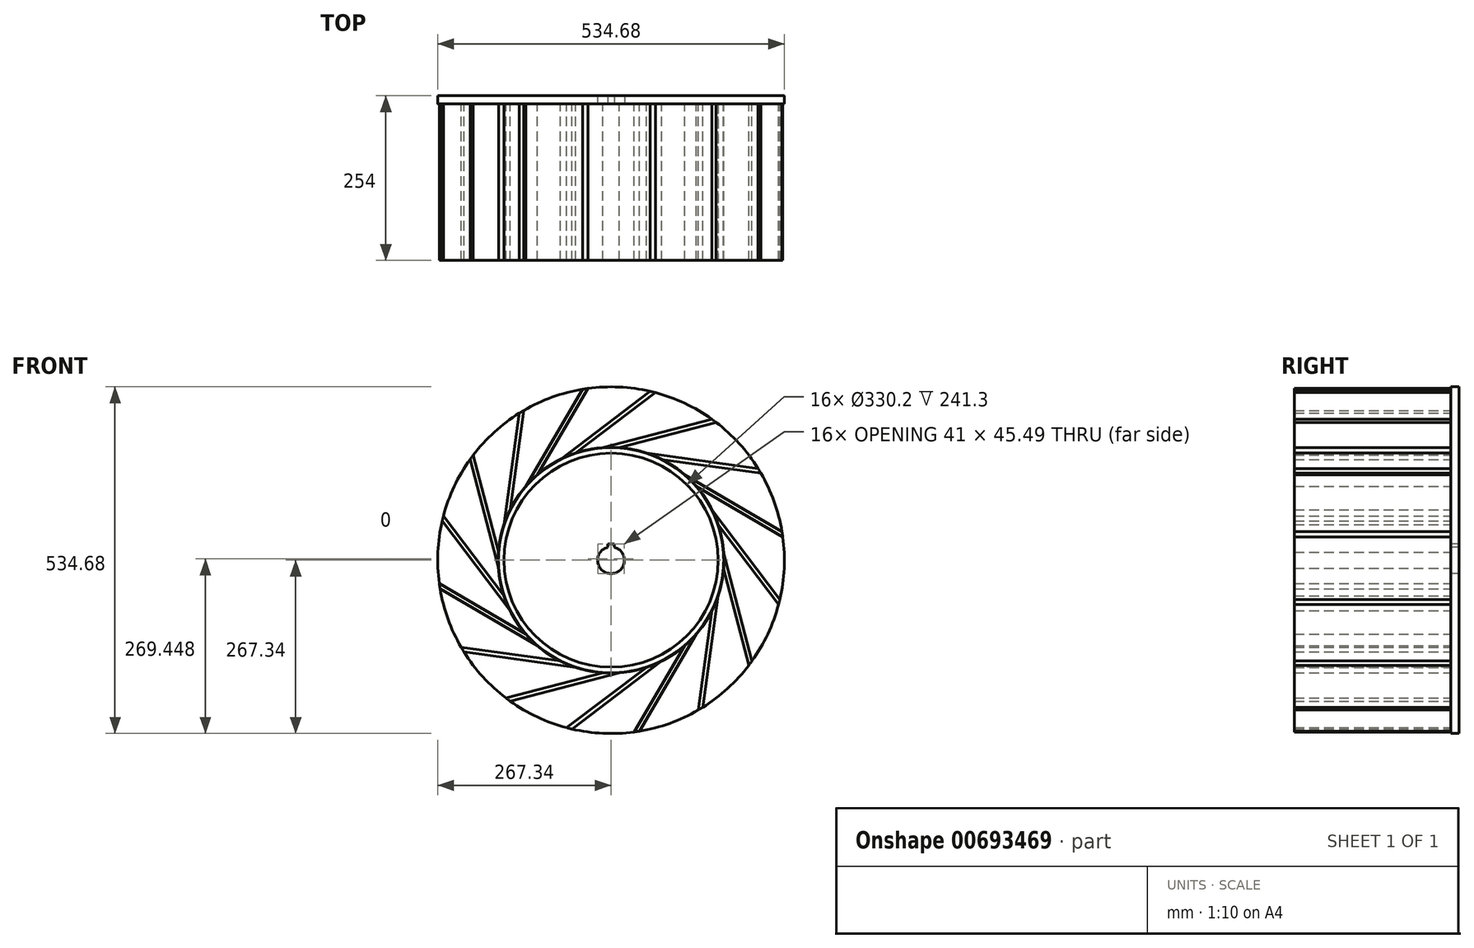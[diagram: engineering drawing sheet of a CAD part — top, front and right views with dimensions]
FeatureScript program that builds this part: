
annotation { "Feature Type Name" : "Feature", "Feature Type Description" : "" }
export const myFeature = defineFeature(function(context is Context, id is Id, definition is map)
    precondition{}
    {
        {
            var Q0;
            Q0=qCreatedBy(makeId("Front.planeOp"),FACE);
            var sketch = newSketch(context, id + "F0", { "sketchPlane" : qUnion([Q0])});
            skCircle(sketch, "E0", {"center": v(0, 0) * mm, "radius": 267.33 * mm});
            skSolve(sketch);
        }
        {
            var Q0;
            Q0 = qSketchRegion(id + "F0", true);
            extrude(context, id + "F1", {"entities" : qUnion([Q0]), "depth" : 12.7 * mm, "offsetDistance" : 25.4 * mm});
        }
        {
            var Q0;
            Q0=makeQuery(id+"F1.opExtrude","CAP_FACE",FACE,{"disambiguationData":[OSD([sQuery(id+"F0.wireOp",EDGE,"E0")])],"isStart":false});
            var sketch = newSketch(context, id + "F2", { "sketchPlane" : qUnion([Q0])});
            skCircle(sketch, "E1", {"center": v(0, 0) * mm, "radius": 173.99 * mm});
            skSolve(sketch);
        }
        {
            var Q0;
            Q0=makeQuery(id+"F2.imprint","IMPRINT",FACE,{"disambiguationData":[TD([[makeQuery(id+"F2.imprint","IMPRINT",EDGE,{"derivedFrom":sQuery(id+"F2.wireOp",EDGE,"E1")}),1.0]])]});
            extrude(context, id + "F3", {"entities" : qUnion([Q0]), "operationType" : NewBodyOperationType.ADD, "depth" : 241.3 * mm, "offsetDistance" : 25.4 * mm});
        }
        {
            var Q0;
            Q0=makeQuery(id+"F1.opExtrude","CAP_FACE",FACE,{"disambiguationData":[OSD([sQuery(id+"F0.wireOp",EDGE,"E0")])],"isStart":false});
            var sketch = newSketch(context, id + "F4", { "sketchPlane" : qUnion([Q0])});
            skLineSegment(sketch, "E2", {"start": v(-12.55, 173.54) * mm, "end": v(155.46, 217.49) * mm});
            skLineSegment(sketch, "E3", {"start": v(12.55, 173.54) * mm, "end": v(162.02, 212.64) * mm});
            skLineSegment(sketch, "E4", {"start": v(-12.55, 173.54) * mm, "end": v(12.55, 173.54) * mm, "construction": true});
            skLineSegment(sketch, "E5", {"start": v(-267.33, 0) * mm, "end": v(267.33, 0) * mm, "construction": true});
            skSolve(sketch);
        }
        {
            var Q0;
            {var subQ5=sQuery(id+"F4.wireOp",EDGE,"E3");Q0=makeQuery(id+"F4.imprint","IMPRINT",FACE,{"disambiguationData":[TD([[makeQuery(id+"F4.imprint","IMPRINT",EDGE,{"derivedFrom":subQ5}),1.0]])]});}
            extrude(context, id + "F5", {"entities" : qUnion([Q0]), "operationType" : NewBodyOperationType.ADD, "depth" : 241.3 * mm, "offsetDistance" : 25.4 * mm});
        }
        {
            var Q0;
            Q0=qCreatedBy(makeId("Right.planeOp"),FACE);
            var sketch = newSketch(context, id + "F6", { "sketchPlane" : qUnion([Q0])});
            skLineSegment(sketch, "E6", {"start": v(0, 0) * mm, "end": v(-78.6, 0) * mm, "construction": true});
            skSolve(sketch);
        }
        {
            var Q0;
            Q0=makeQuery(id+"F1.opExtrude","SWEPT_BODY",BODY,{"disambiguationData":[OSD([sQuery(id+"F0.wireOp",EDGE,"E0")])]});
            var Q1;
            Q1=sQuery(id+"F6.wireOp",EDGE,"E6");
            circularPattern(context, id + "F7", {"entities" : qUnion([Q0]), "axis" : qUnion([Q1]), "angle" : 360 * degree, "instanceCount" : 16, "equalSpace" : true});
        }
        {
            var Q0;
            {var subQ0=sQuery(id+"F2.wireOp",EDGE,"E1");Q0=makeQuery(id+"F7.opPattern","COPY",FACE,{"derivedFrom":makeQuery(id+"F5.boolean.opBoolean","MERGE",FACE,{"derivedFrom":[makeQuery(id+"F3.opExtrude","CAP_FACE",FACE,{"disambiguationData":[OSD([subQ0])],"isStart":false}),makeQuery(id+"F5.opExtrude","CAP_FACE",FACE,{"disambiguationData":[OSD([sQuery(id+"F0.wireOp",EDGE,"E0"),subQ0,sQuery(id+"F4.wireOp",EDGE,"E2"),sQuery(id+"F4.wireOp",EDGE,"E3")])],"isStart":false})]}),"instanceName":"13"});}
            var sketch = newSketch(context, id + "F8", { "sketchPlane" : qUnion([Q0])});
            skCircle(sketch, "E7", {"center": v(0, 0) * mm, "radius": 20.64 * mm});
            skLineSegment(sketch, "E8.bottom", {"start": v(-4.76, 15.33) * mm, "end": v(4.76, 15.33) * mm});
            skLineSegment(sketch, "E8.top", {"start": v(-4.76, 24.85) * mm, "end": v(4.76, 24.85) * mm});
            skLineSegment(sketch, "E8.left", {"start": v(-4.76, 15.33) * mm, "end": v(-4.76, 24.85) * mm});
            skLineSegment(sketch, "E8.right", {"start": v(4.76, 15.33) * mm, "end": v(4.76, 24.85) * mm});
            skLineSegment(sketch, "E9", {"start": v(-20.64, -20.64) * mm, "end": v(20.64, -20.64) * mm, "construction": true});
            skPoint(sketch, "E10", {"position": v(0, -20.64) * mm});
            skSolve(sketch);
        }
        {
            var Q0;
            Q0 = qSketchRegion(id + "F8", true);
            extrude(context, id + "F9", {"entities" : qUnion([Q0]), "operationType" : NewBodyOperationType.REMOVE, "endBound" : BoundingType.UP_TO_NEXT, "oppositeDirection" : true, "depth" : 25.4 * mm, "offsetDistance" : 25.4 * mm});
        }
        {
            var Q0;
            {var subQ0=sQuery(id+"F2.wireOp",EDGE,"E1");Q0=makeQuery(id+"F5.boolean.opBoolean","MERGE",FACE,{"derivedFrom":[makeQuery(id+"F3.opExtrude","CAP_FACE",FACE,{"disambiguationData":[OSD([subQ0])],"isStart":false}),makeQuery(id+"F5.opExtrude","CAP_FACE",FACE,{"disambiguationData":[OSD([sQuery(id+"F0.wireOp",EDGE,"E0"),subQ0,sQuery(id+"F4.wireOp",EDGE,"E2"),sQuery(id+"F4.wireOp",EDGE,"E3")])],"isStart":false})]});}
            var sketch = newSketch(context, id + "F10", { "sketchPlane" : qUnion([Q0])});
            skCircle(sketch, "E11", {"center": v(0, 0) * mm, "radius": 165.1 * mm});
            skSolve(sketch);
        }
        {
            var Q0;
            Q0 = qSketchRegion(id + "F10", true);
            extrude(context, id + "F11", {"entities" : qUnion([Q0]), "operationType" : NewBodyOperationType.REMOVE, "oppositeDirection" : true, "depth" : 241.3 * mm, "offsetDistance" : 25.4 * mm});
        }
    });
